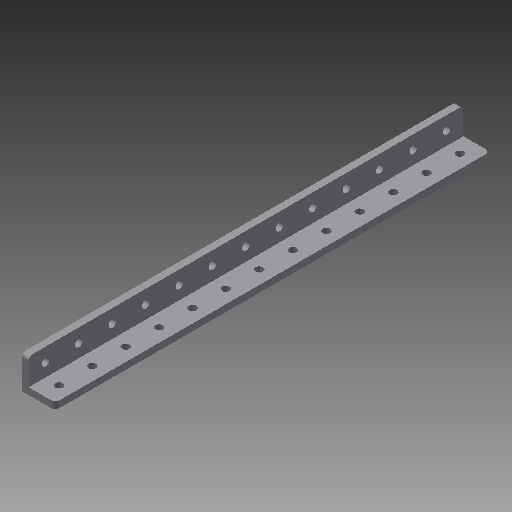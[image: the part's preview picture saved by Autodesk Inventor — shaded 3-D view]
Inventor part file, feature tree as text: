
AUTODESK INVENTOR PART (.ipt)
format: ipt  version: 2019 (Build 230136000, 136)  size: 159,744 bytes
history: native  units: in
note: dims shown in document units (in); Inventor stores cm internally (conversion verified against a paired STEP export)
features: other x1, imported_body x1, extrude x1, fillet x1, sketch x1
ambient origin geometry x8: Origin, YZ Plane, XZ Plane, XY Plane, X Axis, Y Axis, Z Axis, Center Point
bodies: Body1 (feature_tree)
feature tree (5):
  other  "ANGLE_288_2011"
  imported_body  "Base1"
  extrude  "Extrusion1"  Depth=0.0787in
  fillet  "Fillet1"  [1 undecoded]
  sketch  "Sketch1"  dims[d0=0.3937in d1=0.0in d2=0.0787in]
note: 1 required parameter value undecoded (feature->parameter linkage not recoverable at this tier; creation-order binding heuristic only, values carry confidence <= 0.55)
